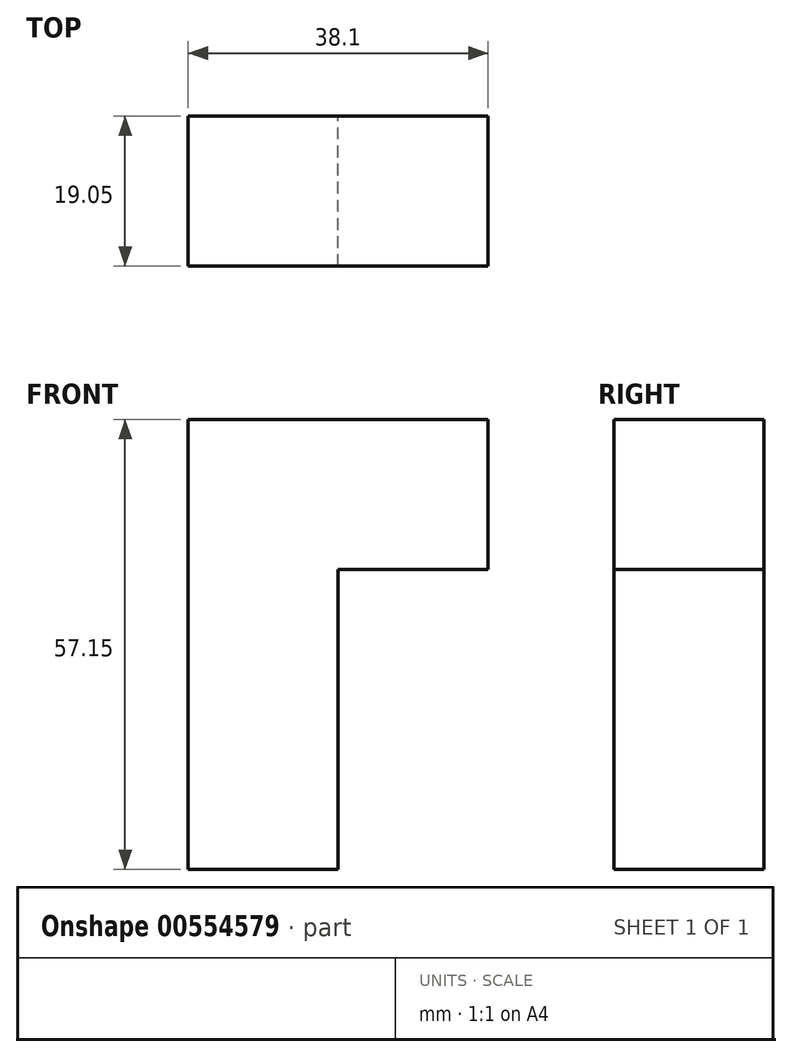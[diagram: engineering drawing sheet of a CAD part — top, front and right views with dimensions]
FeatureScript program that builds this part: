
annotation { "Feature Type Name" : "Feature", "Feature Type Description" : "" }
export const myFeature = defineFeature(function(context is Context, id is Id, definition is map)
    precondition{}
    {
        {
            var Q0;
            Q0=qCreatedBy(makeId("Front.planeOp"),FACE);
            var sketch = newSketch(context, id + "F0", { "sketchPlane" : qUnion([Q0])});
            skLineSegment(sketch, "E0", {"start": v(-31.16, 20.08) * mm, "end": v(-31.16, -37.07) * mm});
            skLineSegment(sketch, "E1", {"start": v(-31.16, -37.07) * mm, "end": v(-12.1, -37.07) * mm});
            skLineSegment(sketch, "E2", {"start": v(-12.1, -37.07) * mm, "end": v(-12.1, 1.03) * mm});
            skLineSegment(sketch, "E3", {"start": v(-12.1, 1.03) * mm, "end": v(6.94, 1.03) * mm});
            skLineSegment(sketch, "E4", {"start": v(6.94, 1.03) * mm, "end": v(6.94, 20.08) * mm});
            skLineSegment(sketch, "E5", {"start": v(6.94, 20.08) * mm, "end": v(-31.16, 20.08) * mm});
            skSolve(sketch);
        }
        {
            var Q0;
            Q0 = qSketchRegion(id + "F0", true);
            extrude(context, id + "F1", {"entities" : qUnion([Q0]), "depth" : 19.05 * mm, "offsetDistance" : 25.4 * mm});
        }
    });
